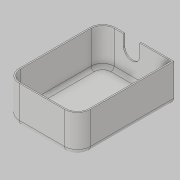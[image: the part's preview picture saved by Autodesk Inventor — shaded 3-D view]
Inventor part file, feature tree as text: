
AUTODESK INVENTOR PART (.ipt)
format: ipt  version: 2018.3 (Build 223284000, 284)  size: 227,328 bytes
history: native  units: in
note: dims shown in document units (in); Inventor stores cm internally (conversion verified against a paired STEP export)
features: sketch x7, extrude x6, fillet x5, shell x1
ambient origin geometry x8: Origin, YZ Plane, XZ Plane, XY Plane, X Axis, Y Axis, Z Axis, Center Point
bodies: Solid1 (feature_tree), Body (feature_tree)
feature tree (19):
  fillet  "Fillet6"  Radius=5.9055in
  fillet  "Fillet4"  Radius=4.362in
  fillet  "Fillet2"  Radius=2.2835in
  shell  "Shell1"  Thickness=0.2134in
  extrude  "Cut_Ethernet"  Depth=0.6181in
  extrude  "Cut_USB1"  Depth=0.126in
  extrude  "Cut_USB2"  Depth=0.1638in
  fillet  "Fillet10"  Radius=0.6252in
  fillet  "Fillet9"  Radius=0.5315in
  extrude  "Extrusion13"  Depth=0.3937in TaperAngle=0.0deg
  extrude  "Extrusion14"  Depth=0.5in TaperAngle=0.0deg
  extrude  "Extrusion16"  Depth=0.5in TaperAngle=0.0deg
  sketch  "Sketch1"  dims[d18=0.5236in d19=0.6181in]
  sketch  "Sketch4"  dims[d20=0.185in d21=0.126in d22=0.5236in]
  sketch  "Sketch5"  dims[d23=0.6181in d24=0.1638in d25=0.6252in d26=0.5315in]
  sketch  "Sketch6"  dims[d27=0.126in d29=0.2134in d30=0.3937in d31=0.0in]
  sketch  "Sketch13"  dims[d32=0.185in d33=0.2134in d34=0.5236in d35=0.6181in d36=0.5in d37=0.0in]
  sketch  "Sketch15"  dims[d38=0.6252in d39=0.5315in d40=0.1732in d41=0.5in d42=0.0in]
  sketch  "Sketch17"  dims[d58=0.7874in d60=0.7874in d62=0.1638in d64=0.7874in d93=0.3228in d94=0.0787in d95=0.0in d96=1.5748in d97=0.2134in d98=0.2134in d101=0.315in d102=0.0787in d103=0.1969in d104=0.1969in d105=1.125in d106=0.3228in d107=1.5748in d108=0.1969in d109=1.125in d110=0.0787in d111=0.0in d117=1.0in d118=0.0787in d119=0.0in d124=1.0in]
